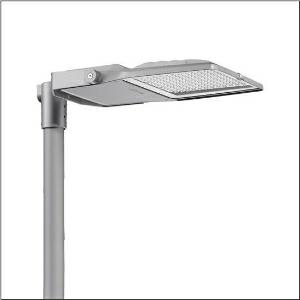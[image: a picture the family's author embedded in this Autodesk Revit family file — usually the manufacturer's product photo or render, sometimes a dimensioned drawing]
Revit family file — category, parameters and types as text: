
# Revit family: floodlight_fl_21_iq_midi___pl64_5xa7781e2e3a_93f0
name_source: partatom
category: Lighting Fixtures
units: mm (PartAtom-declared; Revit-internal decimal feet)

## family parameters
Cut with Voids When Loaded = No
Host = Face
Light Source = No
Part Type = Normal
Room Calculation Point = No
Round Connector Dimension = Use Diameter
Shared = No

## types (1)
- --- (1 x LED, 25930 lm, 208.1 W, 3000K)
    Apparent Load = 208 VA
    CIE Flux Codes = 28 80 98 100 100
    Color Rendering = 70
    Color Temperature = 3000K
    Default Elevation = 1800 mm
    Description = Floodlight FL 21 iQ midi, floodlight, primary light control with lens, of PMMA, primary optical cover: protective disc, of toughened safety glass, transparent, light distribution: PL64, light emission: direct distribution, installation type: surface-mounted, LED, High Power LED, rated luminous flux: 25.930lm, luminous efficacy: 125lm/W, light colour: 730, colour temperature: 3000K, control gear: iQ Comfort/DALI, control: optimised constant luminous flux control (CLO 2.0), Desk-Remote (wireless, voltage-free reading and setting of iQ features in the workshop via application-optimized NFC function/RFID function), Light-Fading, Smart-Wire, Night-Set, Lumen-Switch, Temp-Guard, Auto-Match, with terminal, 6-pole, mains connection: 220..240V, AC, 50/60Hz, start of lifetime: 208W, end of service life: 227W, reduction: 90W, luminaire housing, of diecast aluminium, powder-coated, Siteco® metallic grey (DB 702S), corrosivity category C5 mid according to DIN EN ISO 12944, suitable for swimming pools, chlorine-resistant, sealing non-destructively replaceable, please order mast flange separately, mast bracket, of steel, galvanised, powder-coated, Siteco® metallic grey (DB 702S), protection rating (complete): IP66, insulation class (complete): insulation class II (safety insulation), certification: CE, ENEC, VDE, protection symbol: D, impact resistance: IK08, permissible operating ambient temperature: -40..+40°C, permissible operating ambient temperature for outdoor applications: -40..+50°C, standard: DIN EN 12944, LABS conformity tested according to VDMA 24364:2018-05, packaging unit: 1 piece

Light Distribution: PL64
    Height = 76 mm
    Lamp = 1 x LED
    Lamp Light Flux = 25930 lm
    Lamp Power = 208.1 W
    Lamp count = 1
    Length = 657 mm
    Luminous efficacy = 125 lm/W
    Manufacturer = Siteco
    ModVariant = No
    Model = 5XA7781E2E3A
    Number of Poles = 1
    OnlyDefault = Yes
    Power Factor = 1
    Product Name = Floodlight FL 21 iQ midi | PL64
    Product group = floodlight | pylon annexe
    ProductGroupID = 6201
    Protection Class = Protection class II
    Protection Degree = IP 66
    RLX_Detail_Level = 1
    RLX_Emergency_Light_Flux = 0 lm
    RLX_Emergency_Type = 0
    RLX_Emergency_Type_DB = No
    RlxData = <blob elided: 153805 chars, md5=70bd6fc4>
    Socket = socket
    Standby Power = 0 W
    System Light Flux = 25930 lm
    System Power = 208 W
    Type Comments = factory setting: luminous flux: 100 % | dim-lin: 254 | 710 mA
    Type Image = l_1007123.jpg
    URL = http://relux.com
    VarID = @adj_128719
    Voltage = 0 V
    Weight = 0.00 kg
    Width = 442 mm

## geometry (parser evidence)
native form markers: Blend x4, Sweep x16
no freeform markers — native parametric forms only
